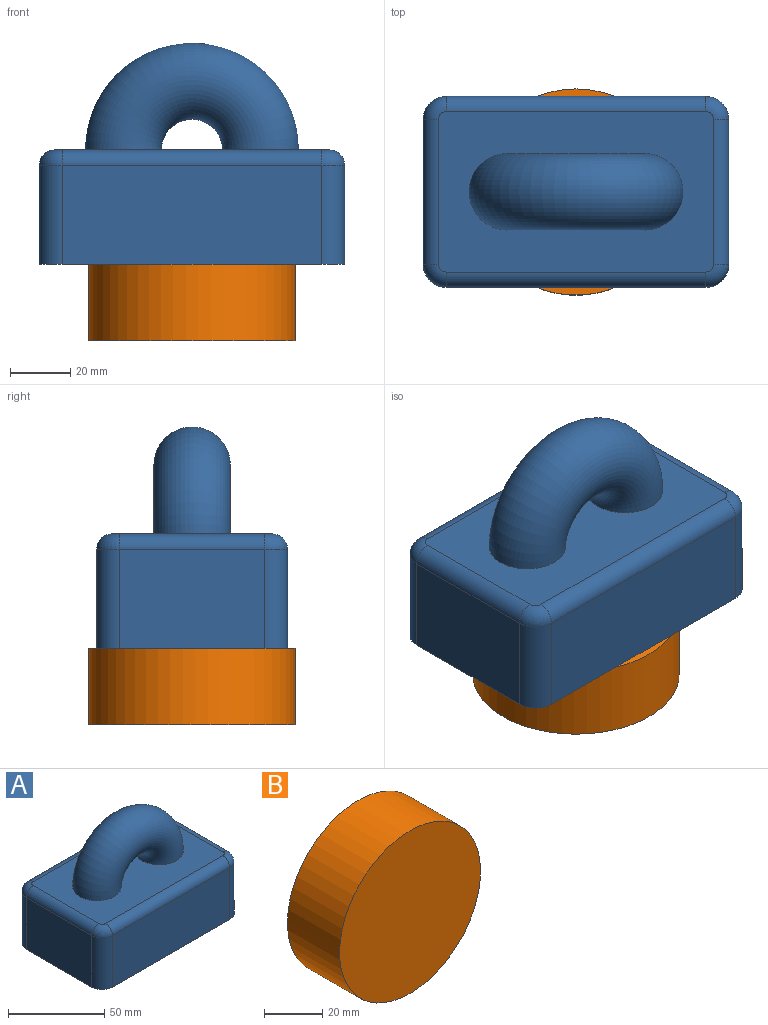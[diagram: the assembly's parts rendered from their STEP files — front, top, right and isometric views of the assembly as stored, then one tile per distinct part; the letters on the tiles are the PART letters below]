
ASSEMBLY  parts=2 mates=2
PART A: 37 faces, bbox 101.6x63.5x76.6 mm
  f0: plane 101.6x63.5mm, normal (0,0,-1), area 785.2mm2, adj f1,f2,f3,f4,f5,f6,f7,f8
  f1: plane 48.26x33.02mm, normal (1,0,0), area 1593.5mm2, adj f0,f2,f8,f13
  f2: cylinder r=7.62mm len=33.02mm, axis (0,0,-1), area 395.2mm2, adj f0,f1,f3,f15
  f3: plane 86.36x33.02mm, normal (0,1,0), area 2851.6mm2, adj f0,f2,f4,f17
  f4: cylinder r=7.62mm len=33.02mm, axis (0,0,-1), area 395.2mm2, adj f0,f3,f5,f16
  f5: plane 48.26x33.02mm, normal (-1,0,0), area 1593.5mm2, adj f0,f4,f6,f14
  f6: cylinder r=7.62mm len=33.02mm, axis (0,0,-1), area 395.2mm2, adj f0,f5,f7,f12
  f7: plane 86.36x33.02mm, normal (0,-1,0), area 2851.6mm2, adj f0,f6,f8,f10
  f8: cylinder r=7.62mm len=33.02mm, axis (0,0,-1), area 395.2mm2, adj f0,f1,f7,f11
  f9: plane 91.44x53.34mm, normal (0,0,1), area 3858.5mm2, adj f10,f11,f12,f13,f14,f15,f16,f17
  f10: cylinder r=5.08mm len=86.36mm, axis (-1,0,0), area 689.1mm2, adj f7,f9,f11,f12
  f11: torus R=2.54mm, axis (0,0,1), area 72.4mm2, adj f8,f9,f10,f13
  f12: torus R=2.54mm, axis (0,0,1), area 72.4mm2, adj f6,f9,f10,f14
  f13: cylinder r=5.08mm len=48.26mm, axis (0,-1,0), area 385.1mm2, adj f1,f9,f11,f15
  f14: cylinder r=5.08mm len=48.26mm, axis (0,1,0), area 385.1mm2, adj f5,f9,f12,f16
  f15: torus R=2.54mm, axis (0,0,1), area 72.4mm2, adj f2,f9,f13,f17
  f16: torus R=2.54mm, axis (0,0,1), area 72.4mm2, adj f4,f9,f14,f17
  f17: cylinder r=5.08mm len=86.36mm, axis (1,0,0), area 689.1mm2, adj f3,f9,f15,f16
  f18: torus R=22.86mm, axis (0,-1,0), area 5730.7mm2, adj f9
  f19: plane 48.26x33.02mm, normal (-1,0,0), area 1593.5mm2, adj f0,f20,f26,f31
  f20: cylinder r=5.08mm len=33.02mm, axis (0,0,-1), area 263.5mm2, adj f0,f19,f21,f33
  f21: plane 86.36x33.02mm, normal (0,-1,0), area 2851.6mm2, adj f0,f20,f22,f35
  f22: cylinder r=5.08mm len=33.02mm, axis (0,0,-1), area 263.5mm2, adj f0,f21,f23,f34
  f23: plane 48.26x33.02mm, normal (1,0,0), area 1593.5mm2, adj f0,f22,f24,f32
  f24: cylinder r=5.08mm len=33.02mm, axis (0,0,-1), area 263.5mm2, adj f0,f23,f25,f30
  f25: plane 86.36x33.02mm, normal (0,1,0), area 2851.6mm2, adj f0,f24,f26,f28
  f26: cylinder r=5.08mm len=33.02mm, axis (0,0,-1), area 263.5mm2, adj f0,f19,f25,f29
  f27: plane 91.44x53.34mm, normal (0,0,-1), area 4218.3mm2, adj f28,f29,f30,f31,f32,f33,f34,f35
  f28: cylinder r=2.54mm len=86.36mm, axis (-1,0,0), area 344.6mm2, adj f25,f27,f29,f30
  f29: torus R=2.54mm, axis (0,0,1), area 26.1mm2, adj f26,f27,f28,f31
  f30: torus R=2.54mm, axis (0,0,1), area 26.1mm2, adj f24,f27,f28,f32
  f31: cylinder r=2.54mm len=48.26mm, axis (0,-1,0), area 192.5mm2, adj f19,f27,f29,f33
  f32: cylinder r=2.54mm len=48.26mm, axis (0,1,0), area 192.5mm2, adj f23,f27,f30,f34
  f33: torus R=2.54mm, axis (0,0,1), area 26.1mm2, adj f20,f27,f31,f35
  f34: torus R=2.54mm, axis (0,0,1), area 26.1mm2, adj f22,f27,f32,f35
  f35: cylinder r=2.54mm len=86.36mm, axis (1,0,0), area 344.6mm2, adj f21,f27,f33,f34
  f36: torus R=22.86mm, axis (0,-1,0), area 4909.5mm2, adj f27
PART B: 3 faces, bbox 68.6x25.4x68.6 mm
  f0: cylinder r=34.3mm len=68.6mm, axis (0,1,0), area 5473.8mm2, adj f1,f2
  f1: plane 68.6x68.6mm, normal (0,-1,0), area 3695.7mm2, adj f0
  f2: plane 68.6x68.6mm, normal (0,1,0), area 3695.7mm2, adj f0
PLACE A at identity fixed
PLACE B rot(axis=(1,0,0),90deg) t=(-2.43,0,0)mm
MATE fastened B.f0 <-> A.f0  axis (0,0,1) through (0,0,0)mm
MATE slider B.f0 <-> A.f0  axis (0,0,1) through (0,0,0)mm
